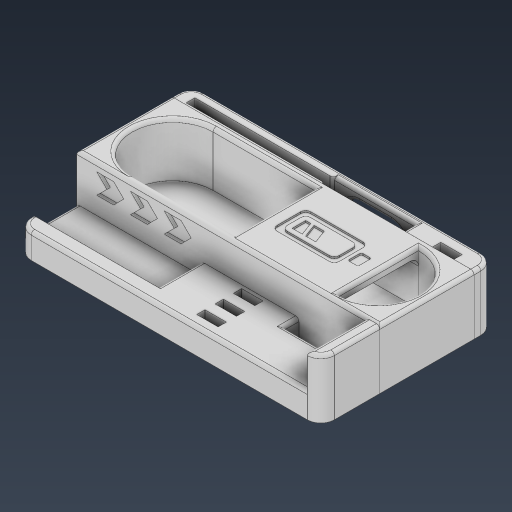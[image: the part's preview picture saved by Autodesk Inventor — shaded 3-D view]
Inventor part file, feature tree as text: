
AUTODESK INVENTOR PART (.ipt)
format: ipt  version: 2024.2 (Build 282272000, 272)  size: 541,696 bytes
history: native  units: mm
features: extrude x15, sketch x8, other x3, projected_geometry x3, sweep x1, plane x1, fillet x1
ambient origin geometry x8: Origin, YZ Plane, XZ Plane, XY Plane, X Axis, Y Axis, Z Axis, Center Point
bodies: Body1 (feature_tree), Body2 (feature_tree), Body3 (feature_tree)
feature tree (32):
  other  "實體1"
  sketch  "草圖1"
  extrude  "擠出1"  Depth=56.0mm
  extrude  "擠出2"  Depth=180.0mm
  sketch  "草圖2"
  extrude  "擠出3"  Depth=35.0mm
  sweep  "掃掠1"
  extrude  "擠出6"  Depth=35.0mm TaperAngle=0.0deg
  extrude  "擠出7"  Depth=5.0mm
  extrude  "擠出8"  Depth=5.0mm
  extrude  "擠出9"  Depth=48.0mm
  extrude  "擠出10"  Depth=32.0mm TaperAngle=0.0deg
  plane  "工作平面3"
  sketch  "草圖7"
  extrude  "擠出11"  Depth=32.0mm TaperAngle=0.0deg
  extrude  "擠出13"  TaperAngle=0.0deg  [1 undecoded]
  extrude  "擠出14"  Depth=5.0mm
  extrude  "擠出15"  Depth=5.0mm
  sketch  "草圖10"
  extrude  "擠出16"  Depth=12.0mm
  fillet  "圓角1"  Radius=8.0mm
  extrude  "擠出17"  Depth=25.0mm TaperAngle=0.0deg
  extrude  "擠出18"  Depth=7.2mm
  projected_geometry  "投影迴路1"
  sketch  "3D 草圖2"
  other  "實體2"
  other  "實體3"
  sketch  "草圖6"
  projected_geometry  "投影迴路5"
  sketch  "草圖8"
  sketch  "草圖9"
  projected_geometry  "投影迴路6"
note: 1 required parameter value undecoded (feature->parameter linkage not recoverable at this tier; creation-order binding heuristic only, values carry confidence <= 0.55)
